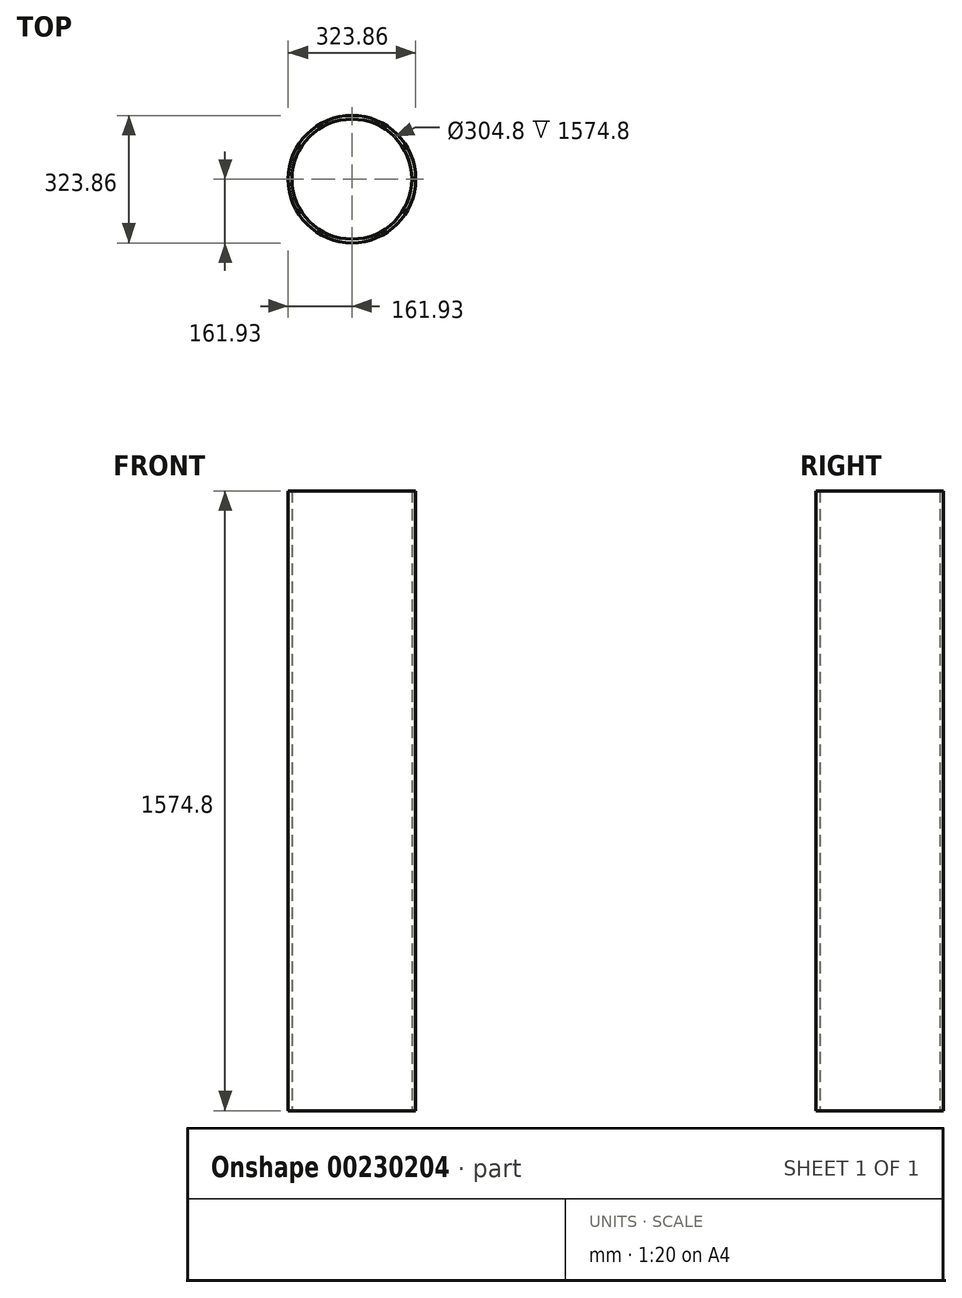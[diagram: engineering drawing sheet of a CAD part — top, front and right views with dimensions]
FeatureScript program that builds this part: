
annotation { "Feature Type Name" : "Feature", "Feature Type Description" : "" }
export const myFeature = defineFeature(function(context is Context, id is Id, definition is map)
    precondition{}
    {
        {
            var Q0;
            Q0=qCreatedBy(makeId("Top.planeOp"),FACE);
            var sketch = newSketch(context, id + "F0", { "sketchPlane" : qUnion([Q0])});
            skCircle(sketch, "E0", {"center": v(0, 0) * mm, "radius": 161.93 * mm});
            skCircle(sketch, "E1", {"center": v(0, 0) * mm, "radius": 152.4 * mm});
            skSolve(sketch);
        }
        {
            var Q0;
            Q0 = qSketchRegion(id + "F0", true);
            extrude(context, id + "F1", {"entities" : qUnion([Q0]), "depth" : 1574.8 * mm, "offsetDistance" : 25.4 * mm});
        }
    });
